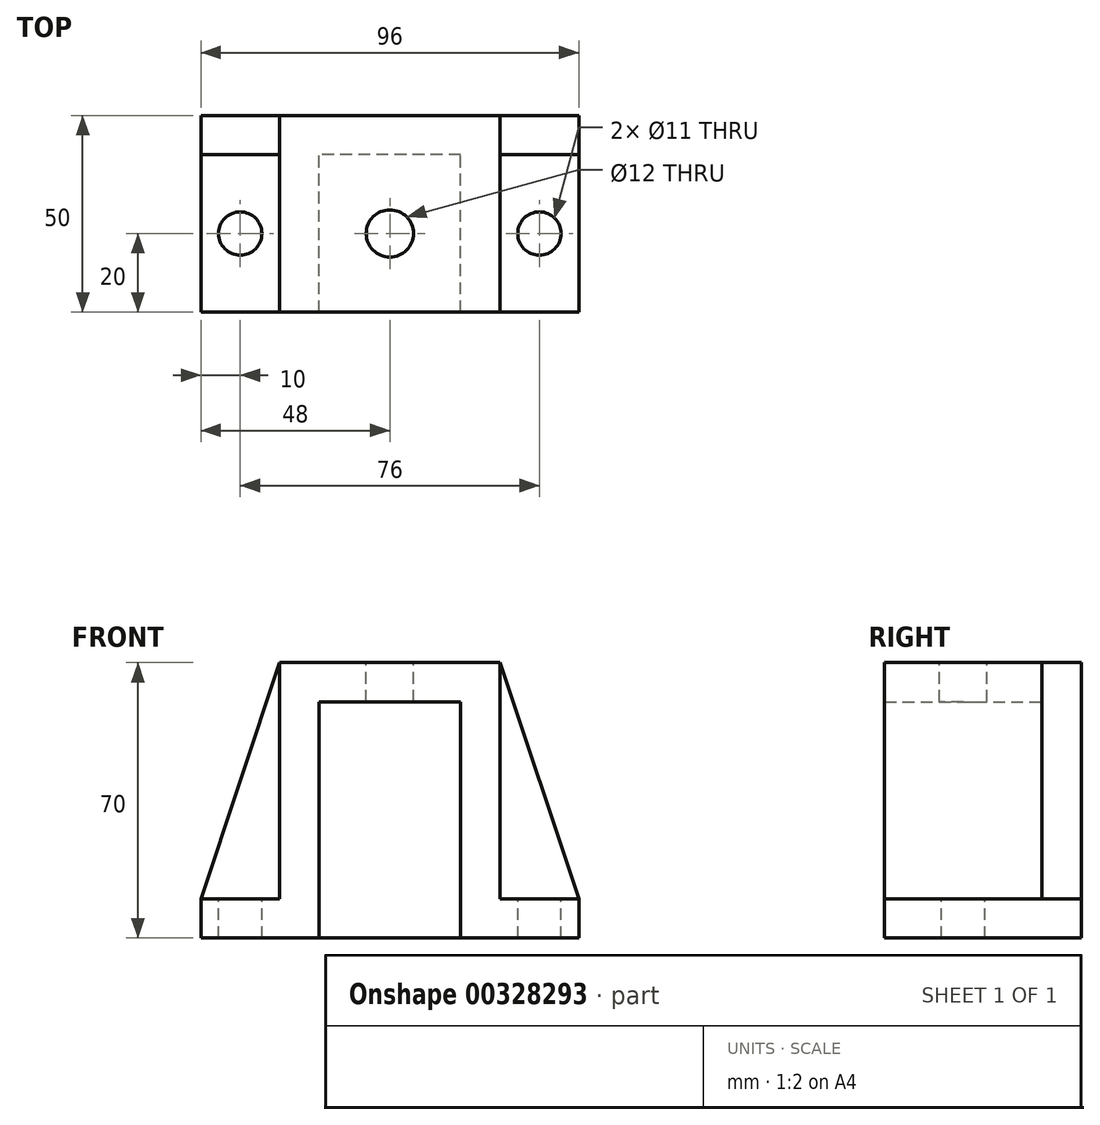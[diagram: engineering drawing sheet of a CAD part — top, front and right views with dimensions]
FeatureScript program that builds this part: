
annotation { "Feature Type Name" : "Feature", "Feature Type Description" : "" }
export const myFeature = defineFeature(function(context is Context, id is Id, definition is map)
    precondition{}
    {
        {
            var Q0;
            Q0=qCreatedBy(makeId("Front.planeOp"),FACE);
            var sketch = newSketch(context, id + "F0", { "sketchPlane" : qUnion([Q0])});
            skLineSegment(sketch, "E0", {"start": v(0, 48.07) * mm, "end": v(-28, 48.07) * mm});
            skLineSegment(sketch, "E1", {"start": v(-28, 48.07) * mm, "end": v(-48, -11.93) * mm});
            skLineSegment(sketch, "E2", {"start": v(-48, -11.93) * mm, "end": v(-48, -21.93) * mm});
            skLineSegment(sketch, "E3", {"start": v(-48, -21.93) * mm, "end": v(0, -21.93) * mm});
            skLineSegment(sketch, "E4", {"start": v(-28, 48.07) * mm, "end": v(-28, -11.93) * mm});
            skLineSegment(sketch, "E5", {"start": v(-28, -11.93) * mm, "end": v(-48, -11.93) * mm});
            skLineSegment(sketch, "E6", {"start": v(0, 38.07) * mm, "end": v(-18, 38.07) * mm});
            skLineSegment(sketch, "E7", {"start": v(-18, 38.07) * mm, "end": v(-18, -21.93) * mm});
            skLineSegment(sketch, "E8.MirrorCS", {"start": v(0, 48.07) * mm, "end": v(28, 48.07) * mm});
            skLineSegment(sketch, "E9.MirrorCS", {"start": v(0, 38.07) * mm, "end": v(18, 38.07) * mm});
            skLineSegment(sketch, "E10.MirrorCS", {"start": v(18, 38.07) * mm, "end": v(18, -21.93) * mm});
            skLineSegment(sketch, "E11.MirrorCS", {"start": v(28, 48.07) * mm, "end": v(28, -11.93) * mm});
            skLineSegment(sketch, "E12.MirrorCS", {"start": v(28, 48.07) * mm, "end": v(48, -11.93) * mm});
            skLineSegment(sketch, "E13.MirrorCS", {"start": v(28, -11.93) * mm, "end": v(48, -11.93) * mm});
            skLineSegment(sketch, "E14.MirrorCS", {"start": v(48, -21.93) * mm, "end": v(0, -21.93) * mm});
            skLineSegment(sketch, "E15.MirrorCS", {"start": v(48, -11.93) * mm, "end": v(48, -21.93) * mm});
            skSolve(sketch);
        }
        {
            var Q0;
            Q0=makeQuery(id+"F0.imprint","IMPRINT",FACE,{"disambiguationData":[TD([[makeQuery(id+"F0.imprint","IMPRINT",EDGE,{"derivedFrom":sQuery(id+"F0.wireOp",EDGE,"E0")}),1.0]])]});
            extrude(context, id + "F1", {"entities" : qUnion([Q0]), "depth" : 50 * mm});
        }
        {
            var Q0;
            Q0 = qSketchRegion(id + "F0", true);
            extrude(context, id + "F2", {"entities" : qUnion([Q0]), "operationType" : NewBodyOperationType.ADD, "depth" : 10 * mm});
        }
        {
            var Q0;
            Q0=makeQuery(id+"F1.opExtrude","SWEPT_FACE",FACE,{"disambiguationData":[OSD([sQuery(id+"F0.wireOp",EDGE,"E5")])]});
            var sketch = newSketch(context, id + "F3", { "sketchPlane" : qUnion([Q0])});
            skCircle(sketch, "E16", {"center": v(-38, -30) * mm, "radius": 5.5 * mm});
            skCircle(sketch, "E17.MirrorC", {"center": v(38, -30) * mm, "radius": 5.5 * mm});
            skSolve(sketch);
        }
        {
            var Q0;
            Q0 = qSketchRegion(id + "F3", true);
            extrude(context, id + "F4", {"entities" : qUnion([Q0]), "operationType" : NewBodyOperationType.REMOVE, "oppositeDirection" : true, "depth" : 10 * mm});
        }
        {
            var Q0;
            Q0=makeQuery(id+"F1.opExtrude","SWEPT_FACE",FACE,{"disambiguationData":[OSD([sQuery(id+"F0.wireOp",EDGE,"E0"),sQuery(id+"F0.wireOp",EDGE,"E8.MirrorCS")])]});
            var sketch = newSketch(context, id + "F5", { "sketchPlane" : qUnion([Q0])});
            skCircle(sketch, "E18", {"center": v(0, -30) * mm, "radius": 6 * mm});
            skSolve(sketch);
        }
        {
            var Q0;
            Q0 = qSketchRegion(id + "F5", true);
            extrude(context, id + "F6", {"entities" : qUnion([Q0]), "operationType" : NewBodyOperationType.REMOVE, "oppositeDirection" : true, "depth" : 12 * mm});
        }
    });
